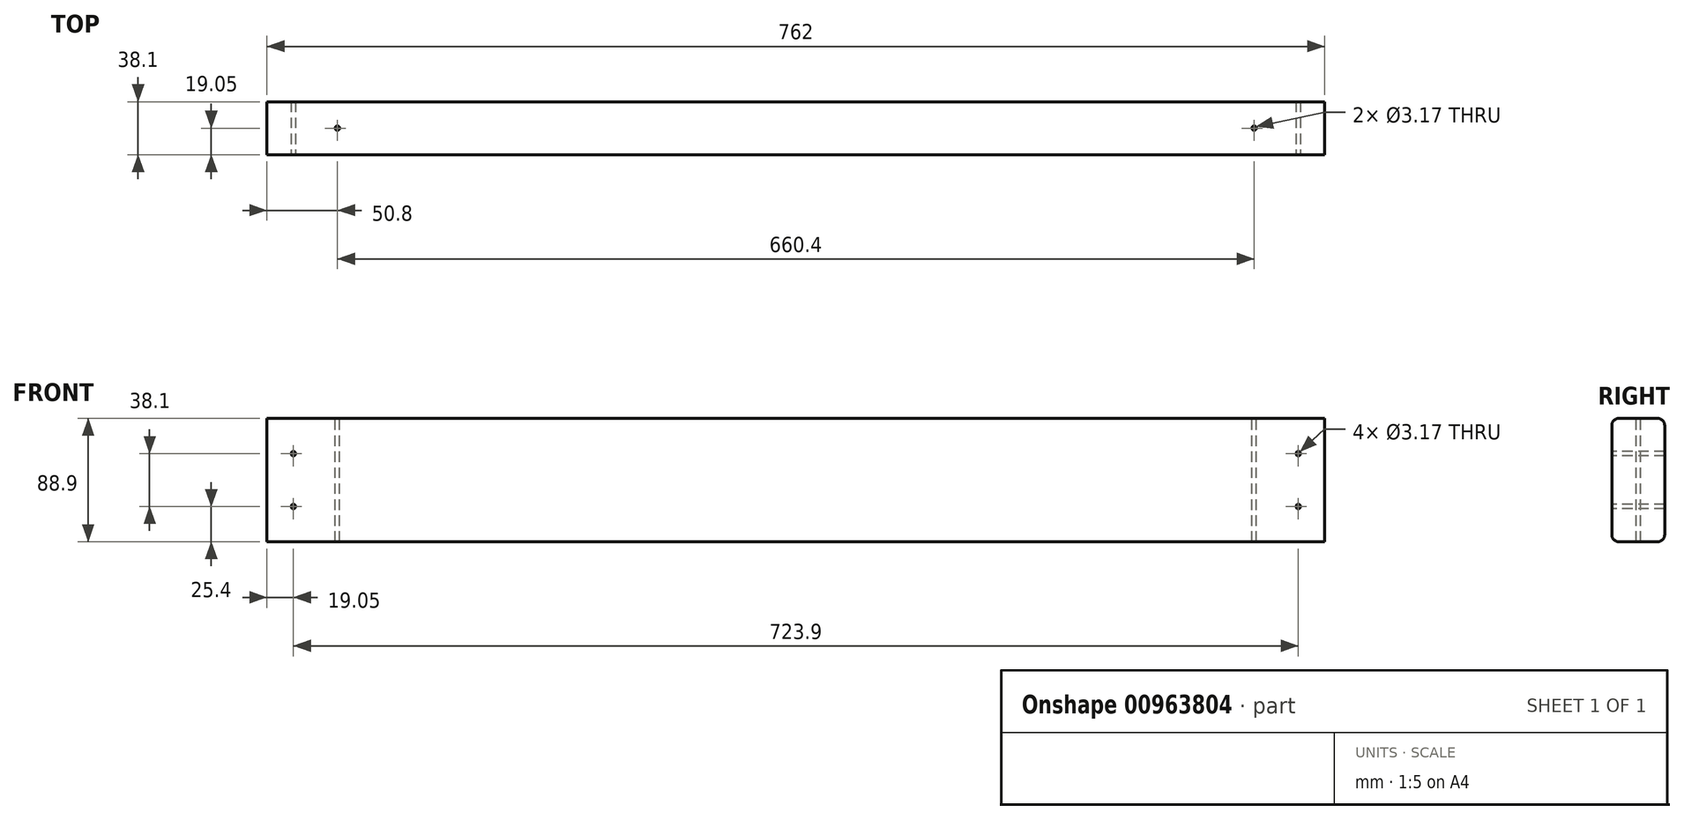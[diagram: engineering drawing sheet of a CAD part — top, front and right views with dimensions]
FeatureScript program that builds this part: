
annotation { "Feature Type Name" : "Feature", "Feature Type Description" : "" }
export const myFeature = defineFeature(function(context is Context, id is Id, definition is map)
    precondition{}
    {
        {
            var Q0;
            Q0=qCreatedBy(makeId("Right.planeOp"),FACE);
            var sketch = newSketch(context, id + "F0", { "sketchPlane" : qUnion([Q0])});
            skLineSegment(sketch, "E0.bottom", {"start": v(19.05, 44.45) * mm, "end": v(-19.05, 44.45) * mm});
            skLineSegment(sketch, "E0.top", {"start": v(19.05, -44.45) * mm, "end": v(-19.05, -44.45) * mm});
            skLineSegment(sketch, "E0.left", {"start": v(19.05, 44.45) * mm, "end": v(19.05, -44.45) * mm});
            skLineSegment(sketch, "E0.right", {"start": v(-19.05, 44.45) * mm, "end": v(-19.05, -44.45) * mm});
            skPoint(sketch, "E0.middle", {"position": v(0, 0) * mm});
            skSolve(sketch);
        }
        {
            var Q0;
            Q0=makeQuery(id+"F0.imprint","IMPRINT",FACE,{"disambiguationData":[TD([[makeQuery(id+"F0.imprint","IMPRINT",EDGE,{"derivedFrom":sQuery(id+"F0.wireOp",EDGE,"E0.bottom")}),1.0]])]});
            extrude(context, id + "F1", {"entities" : qUnion([Q0]), "endBound" : BoundingType.SYMMETRIC, "depth" : 762 * mm, "offsetDistance" : 25.4 * mm});
        }
        {
            var Q0;
            Q0=makeQuery(id+"F1.opExtrude","SWEPT_EDGE",EDGE,{"disambiguationData":[OSD([sQuery(id+"F0.wireOp",EDGE,"E0.bottom"),sQuery(id+"F0.wireOp",EDGE,"E0.right")])]});
            var Q1;
            Q1=makeQuery(id+"F1.opExtrude","SWEPT_EDGE",EDGE,{"disambiguationData":[OSD([sQuery(id+"F0.wireOp",EDGE,"E0.bottom"),sQuery(id+"F0.wireOp",EDGE,"E0.left")])]});
            var Q2;
            Q2=makeQuery(id+"F1.opExtrude","SWEPT_EDGE",EDGE,{"disambiguationData":[OSD([sQuery(id+"F0.wireOp",EDGE,"E0.top"),sQuery(id+"F0.wireOp",EDGE,"E0.right")])]});
            var Q3;
            Q3=makeQuery(id+"F1.opExtrude","SWEPT_EDGE",EDGE,{"disambiguationData":[OSD([sQuery(id+"F0.wireOp",EDGE,"E0.top"),sQuery(id+"F0.wireOp",EDGE,"E0.left")])]});
            fillet(context, id + "F2", {"entities" : qUnion([Q0, Q1, Q2, Q3]), "radius" : 5.08 * mm, "tangentPropagation" : true, "allowEdgeOverflow" : false});
        }
        {
            var Q0;
            Q0=makeQuery(id+"F1.opExtrude","SWEPT_FACE",FACE,{"disambiguationData":[OSD([sQuery(id+"F0.wireOp",EDGE,"E0.bottom")])]});
            var sketch = newSketch(context, id + "F3", { "sketchPlane" : qUnion([Q0])});
            skCircle(sketch, "E1", {"center": v(330.2, 0) * mm, "radius": 1.59 * mm});
            skSolve(sketch);
        }
        {
            var Q0;
            Q0=makeQuery(id+"F3.imprint","IMPRINT",FACE,{"disambiguationData":[TD([[makeQuery(id+"F3.imprint","IMPRINT",EDGE,{"derivedFrom":sQuery(id+"F3.wireOp",EDGE,"E1")}),1.0]])]});
            var Q1;
            Q1=sQuery(id+"F3.wireOp",EDGE,"E1");
            var Q2;
            Q2=makeQuery(id+"F1.opExtrude","SWEPT_FACE",FACE,{"disambiguationData":[OSD([sQuery(id+"F0.wireOp",EDGE,"E0.top")])]});
            extrude(context, id + "F4", {"entities" : qUnion([Q0]), "operationType" : NewBodyOperationType.REMOVE, "surfaceEntities" : qUnion([Q1]), "endBound" : BoundingType.UP_TO_SURFACE, "oppositeDirection" : true, "depth" : 25.4 * mm, "endBoundEntityFace" : qUnion([Q2]), "offsetDistance" : 25.4 * mm});
        }
        {
            var Q0;
            Q0=makeQuery(id+"F1.opExtrude","SWEPT_FACE",FACE,{"disambiguationData":[OSD([sQuery(id+"F0.wireOp",EDGE,"E0.bottom")])]});
            var sketch = newSketch(context, id + "F5", { "sketchPlane" : qUnion([Q0])});
            skCircle(sketch, "E2", {"center": v(-330.2, 0) * mm, "radius": 1.59 * mm});
            skSolve(sketch);
        }
        {
            var Q0;
            Q0=makeQuery(id+"F5.imprint","IMPRINT",FACE,{"disambiguationData":[TD([[makeQuery(id+"F5.imprint","IMPRINT",EDGE,{"derivedFrom":sQuery(id+"F5.wireOp",EDGE,"E2")}),1.0]])]});
            var Q1;
            Q1=sQuery(id+"F5.wireOp",EDGE,"E2");
            var Q2;
            Q2=makeQuery(id+"F1.opExtrude","SWEPT_FACE",FACE,{"disambiguationData":[OSD([sQuery(id+"F0.wireOp",EDGE,"E0.top")])]});
            extrude(context, id + "F6", {"entities" : qUnion([Q0]), "operationType" : NewBodyOperationType.REMOVE, "surfaceEntities" : qUnion([Q1]), "endBound" : BoundingType.UP_TO_SURFACE, "oppositeDirection" : true, "depth" : 25.4 * mm, "endBoundEntityFace" : qUnion([Q2]), "offsetDistance" : 25.4 * mm});
        }
        {
            var Q0;
            Q0=makeQuery(id+"F1.opExtrude","SWEPT_FACE",FACE,{"disambiguationData":[OSD([sQuery(id+"F0.wireOp",EDGE,"E0.right")])]});
            var sketch = newSketch(context, id + "F7", { "sketchPlane" : qUnion([Q0])});
            skCircle(sketch, "E3", {"center": v(-361.95, 19.05) * mm, "radius": 1.59 * mm});
            skSolve(sketch);
        }
        {
            var Q0;
            Q0=makeQuery(id+"F7.imprint","IMPRINT",FACE,{"disambiguationData":[TD([[makeQuery(id+"F7.imprint","IMPRINT",EDGE,{"derivedFrom":sQuery(id+"F7.wireOp",EDGE,"E3")}),-1.0]])]});
            var sketch = newSketch(context, id + "F8", { "sketchPlane" : qUnion([Q0])});
            skCircle(sketch, "E4", {"center": v(-361.95, -19.05) * mm, "radius": 1.59 * mm});
            skSolve(sketch);
        }
        {
            var Q0;
            Q0=makeQuery(id+"F7.imprint","IMPRINT",FACE,{"disambiguationData":[TD([[makeQuery(id+"F7.imprint","IMPRINT",EDGE,{"derivedFrom":sQuery(id+"F7.wireOp",EDGE,"E3")}),-1.0]])]});
            var sketch = newSketch(context, id + "F9", { "sketchPlane" : qUnion([Q0])});
            skCircle(sketch, "E5", {"center": v(361.95, 19.05) * mm, "radius": 1.59 * mm});
            skSolve(sketch);
        }
        {
            var Q0;
            Q0=makeQuery(id+"F7.imprint","IMPRINT",FACE,{"disambiguationData":[TD([[makeQuery(id+"F7.imprint","IMPRINT",EDGE,{"derivedFrom":sQuery(id+"F7.wireOp",EDGE,"E3")}),-1.0]])]});
            var sketch = newSketch(context, id + "F10", { "sketchPlane" : qUnion([Q0])});
            skCircle(sketch, "E6", {"center": v(361.95, -19.05) * mm, "radius": 1.59 * mm});
            skSolve(sketch);
        }
        {
            var Q0;
            Q0 = qSketchRegion(id + "F7", true);
            var Q1;
            Q1 = qSketchRegion(id + "F8", true);
            var Q2;
            Q2 = qSketchRegion(id + "F9", true);
            var Q3;
            Q3 = qSketchRegion(id + "F10", true);
            var Q4;
            Q4=makeQuery(id+"F1.opExtrude","SWEPT_FACE",FACE,{"disambiguationData":[OSD([sQuery(id+"F0.wireOp",EDGE,"E0.left")])]});
            extrude(context, id + "F11", {"entities" : qUnion([Q0, Q1, Q2, Q3]), "operationType" : NewBodyOperationType.REMOVE, "endBound" : BoundingType.UP_TO_SURFACE, "oppositeDirection" : true, "depth" : 25.4 * mm, "endBoundEntityFace" : qUnion([Q4]), "offsetDistance" : 25.4 * mm});
        }
    });
